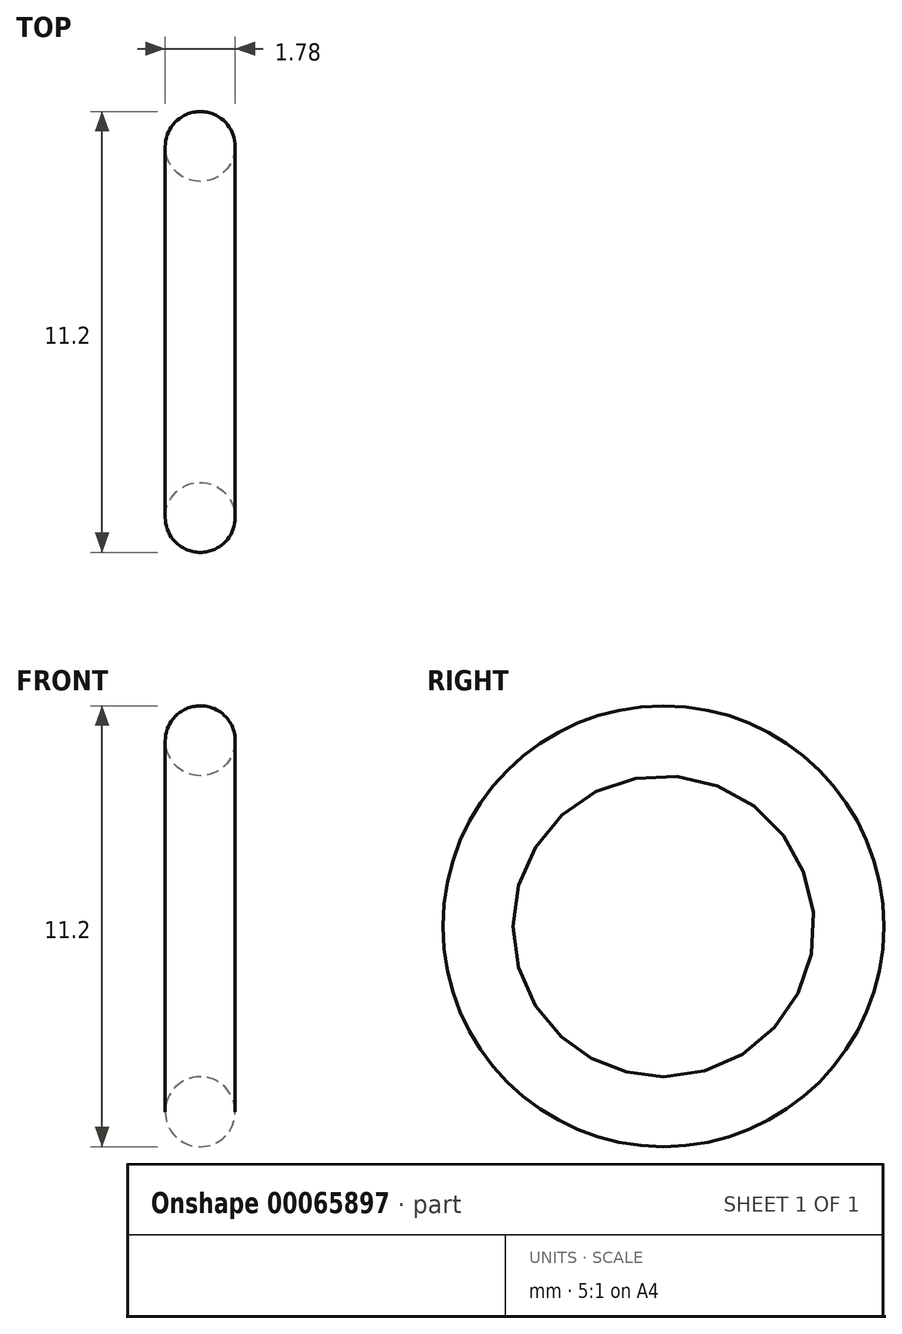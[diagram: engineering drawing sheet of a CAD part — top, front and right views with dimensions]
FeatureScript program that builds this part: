
annotation { "Feature Type Name" : "Feature", "Feature Type Description" : "" }
export const myFeature = defineFeature(function(context is Context, id is Id, definition is map)
    precondition{}
    {
        {
            var Q0;
            Q0=qCreatedBy(makeId("Front.planeOp"),FACE);
            var sketch = newSketch(context, id + "F0", { "sketchPlane" : qUnion([Q0])});
            skLineSegment(sketch, "E0", {"start": v(0, 0) * mm, "end": v(-6.06, 0) * mm, "construction": true});
            skCircle(sketch, "E1", {"center": v(0, 4.71) * mm, "radius": 0.89 * mm});
            skSolve(sketch);
        }
        {
            var Q0;
            Q0=makeQuery(id+"F0.imprint","IMPRINT",FACE,{"disambiguationData":[TD([[makeQuery(id+"F0.imprint","IMPRINT",EDGE,{"derivedFrom":sQuery(id+"F0.wireOp",EDGE,"E1")}),1.0]])]});
            var Q1;
            Q1=sQuery(id+"F0.wireOp",EDGE,"E0");
            revolve(context, id + "F1", {"entities" : qUnion([Q0]), "axis" : qUnion([Q1]), "revolveType" : RevolveType.FULL});
        }
    });
